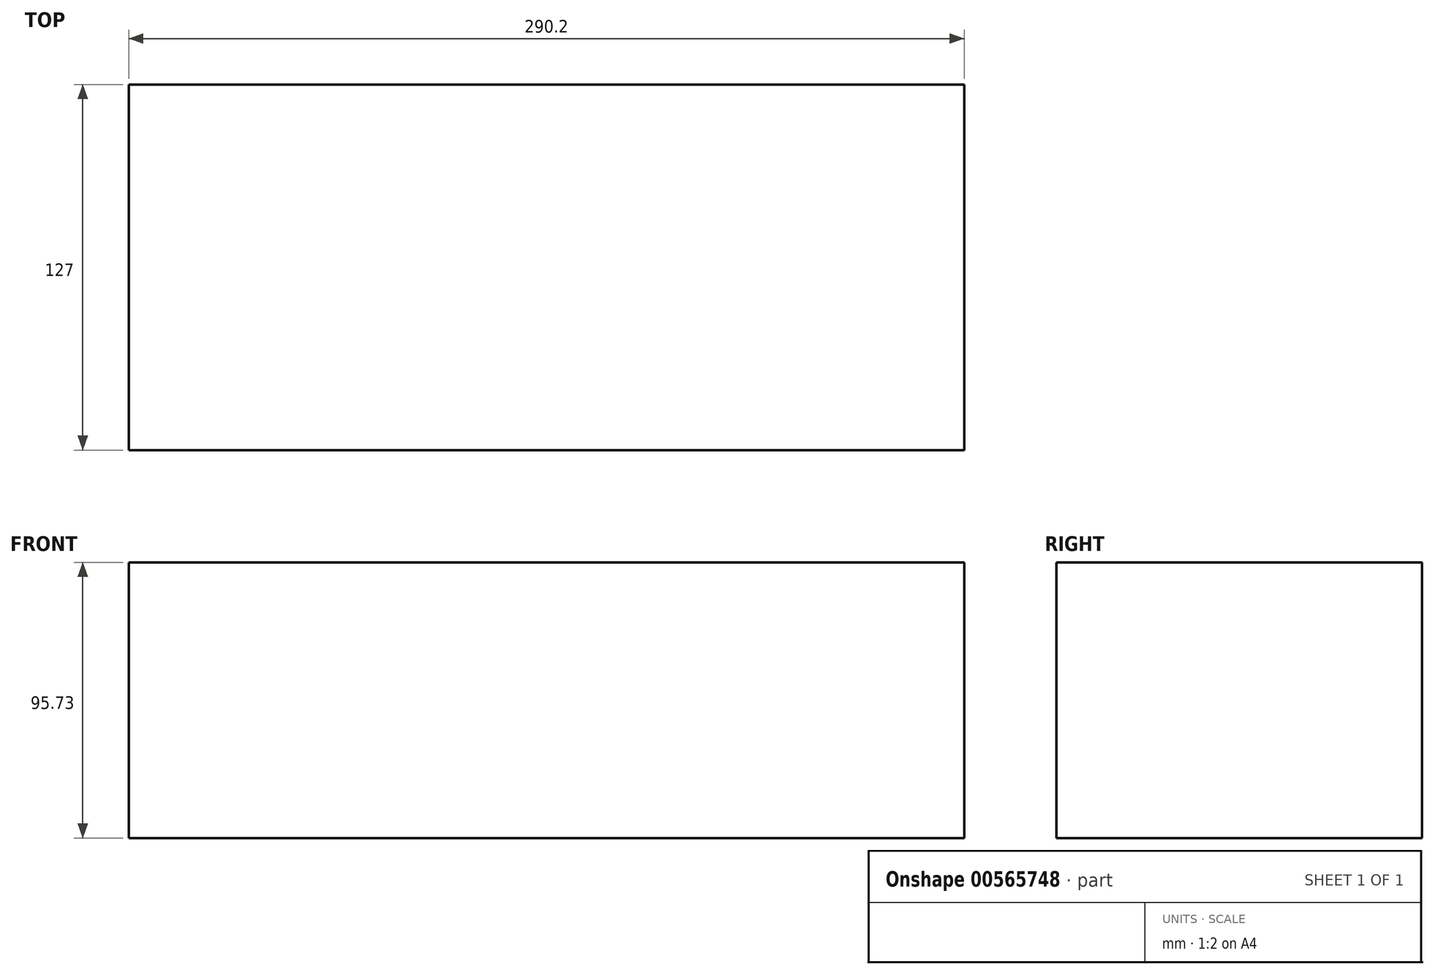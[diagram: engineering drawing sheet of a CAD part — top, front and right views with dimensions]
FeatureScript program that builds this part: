
annotation { "Feature Type Name" : "Feature", "Feature Type Description" : "" }
export const myFeature = defineFeature(function(context is Context, id is Id, definition is map)
    precondition{}
    {
        {
            var Q0;
            Q0=qCreatedBy(makeId("Front.planeOp"),FACE);
            var sketch = newSketch(context, id + "F0", { "sketchPlane" : qUnion([Q0])});
            skLineSegment(sketch, "E0.bottom", {"start": v(-209.4, -105.69) * mm, "end": v(80.8, -105.69) * mm});
            skLineSegment(sketch, "E0.top", {"start": v(-209.4, -9.96) * mm, "end": v(80.8, -9.96) * mm});
            skLineSegment(sketch, "E0.left", {"start": v(-209.4, -105.69) * mm, "end": v(-209.4, -9.96) * mm});
            skLineSegment(sketch, "E0.right", {"start": v(80.8, -105.69) * mm, "end": v(80.8, -9.96) * mm});
            skSolve(sketch);
        }
        {
            var Q0;
            Q0=makeQuery(id+"F0.imprint","IMPRINT",FACE,{"disambiguationData":[TD([[makeQuery(id+"F0.imprint","IMPRINT",EDGE,{"derivedFrom":sQuery(id+"F0.wireOp",EDGE,"E0.bottom")}),1.0]])]});
            extrude(context, id + "F1", {"entities" : qUnion([Q0]), "depth" : 127 * mm, "offsetDistance" : 25.4 * mm});
        }
    });
